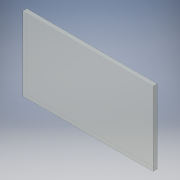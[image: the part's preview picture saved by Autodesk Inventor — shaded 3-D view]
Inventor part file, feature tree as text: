
AUTODESK INVENTOR PART (.ipt)
format: ipt  version: 2016 (Build 200138000, 138)  size: 95,232 bytes
history: native  units: in
note: dims shown in document units (in); Inventor stores cm internally (conversion verified against a paired STEP export)
features: extrude x1, sketch x1
ambient origin geometry x8: Origin, YZ Plane, XZ Plane, XY Plane, X Axis, Y Axis, Z Axis, Center Point
bodies: Solid1 (feature_tree)
feature tree (2):
  extrude  "Extrusion1"  Depth=9.375in
  sketch  "Sketch1"  dims[d0=16.5in d1=9.375in d2=0.5in d3=0.0in]
